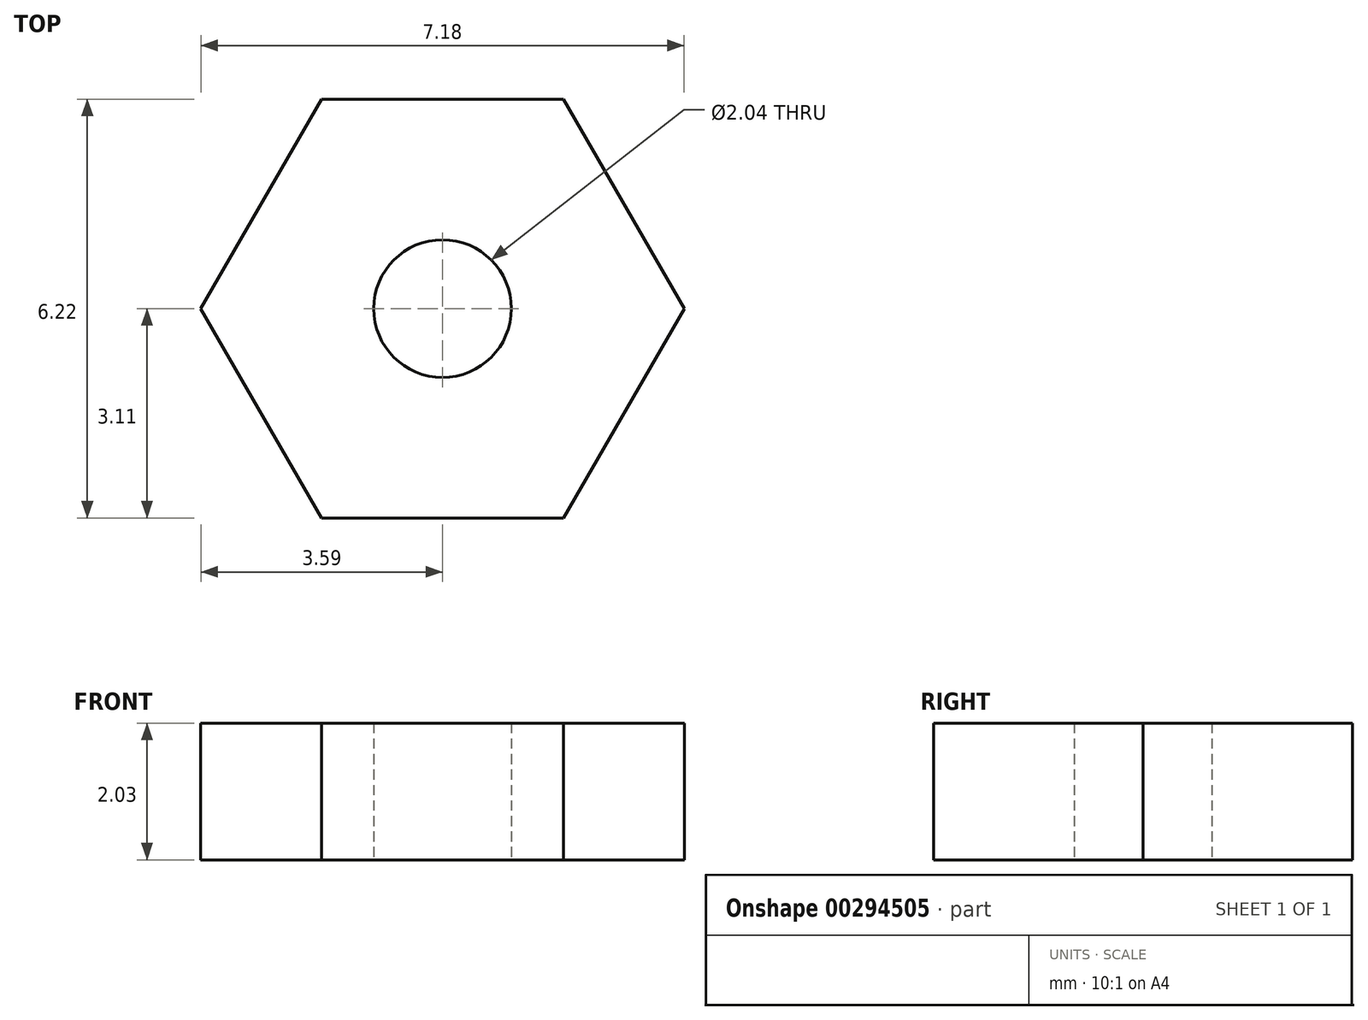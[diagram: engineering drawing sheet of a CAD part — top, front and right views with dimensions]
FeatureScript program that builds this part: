
annotation { "Feature Type Name" : "Feature", "Feature Type Description" : "" }
export const myFeature = defineFeature(function(context is Context, id is Id, definition is map)
    precondition{}
    {
        {
            var Q0;
            Q0=qCreatedBy(makeId("Top.planeOp"),FACE);
            var sketch = newSketch(context, id + "F0", { "sketchPlane" : qUnion([Q0])});
            skCircle(sketch, "E0.cCircle", {"center": v(0, 0) * mm, "radius": 3.11 * mm, "construction": true});
            skLineSegment(sketch, "E0.0", {"start": v(3.6, 0) * mm, "end": v(1.8, -3.11) * mm});
            skLineSegment(sketch, "E0.1", {"start": v(1.8, -3.11) * mm, "end": v(-1.8, -3.11) * mm});
            skLineSegment(sketch, "E0.2", {"start": v(-1.8, -3.11) * mm, "end": v(-3.6, 0) * mm});
            skLineSegment(sketch, "E0.3", {"start": v(-3.6, 0) * mm, "end": v(-1.8, 3.11) * mm});
            skLineSegment(sketch, "E0.4", {"start": v(-1.8, 3.11) * mm, "end": v(1.8, 3.11) * mm});
            skLineSegment(sketch, "E0.5", {"start": v(1.8, 3.11) * mm, "end": v(3.6, 0) * mm});
            skPoint(sketch, "E0.0.midPoint", {"position": v(2.7, -1.56) * mm});
            skCircle(sketch, "E1", {"center": v(0, 0) * mm, "radius": 1.02 * mm});
            skSolve(sketch);
        }
        {
            var Q0;
            Q0=makeQuery(id+"F0.imprint","IMPRINT",FACE,{"disambiguationData":[TD([[makeQuery(id+"F0.imprint","IMPRINT",EDGE,{"derivedFrom":sQuery(id+"F0.wireOp",EDGE,"E0.0")}),-1.0]])]});
            extrude(context, id + "F1", {"entities" : qUnion([Q0]), "depth" : 2.03 * mm});
        }
    });
